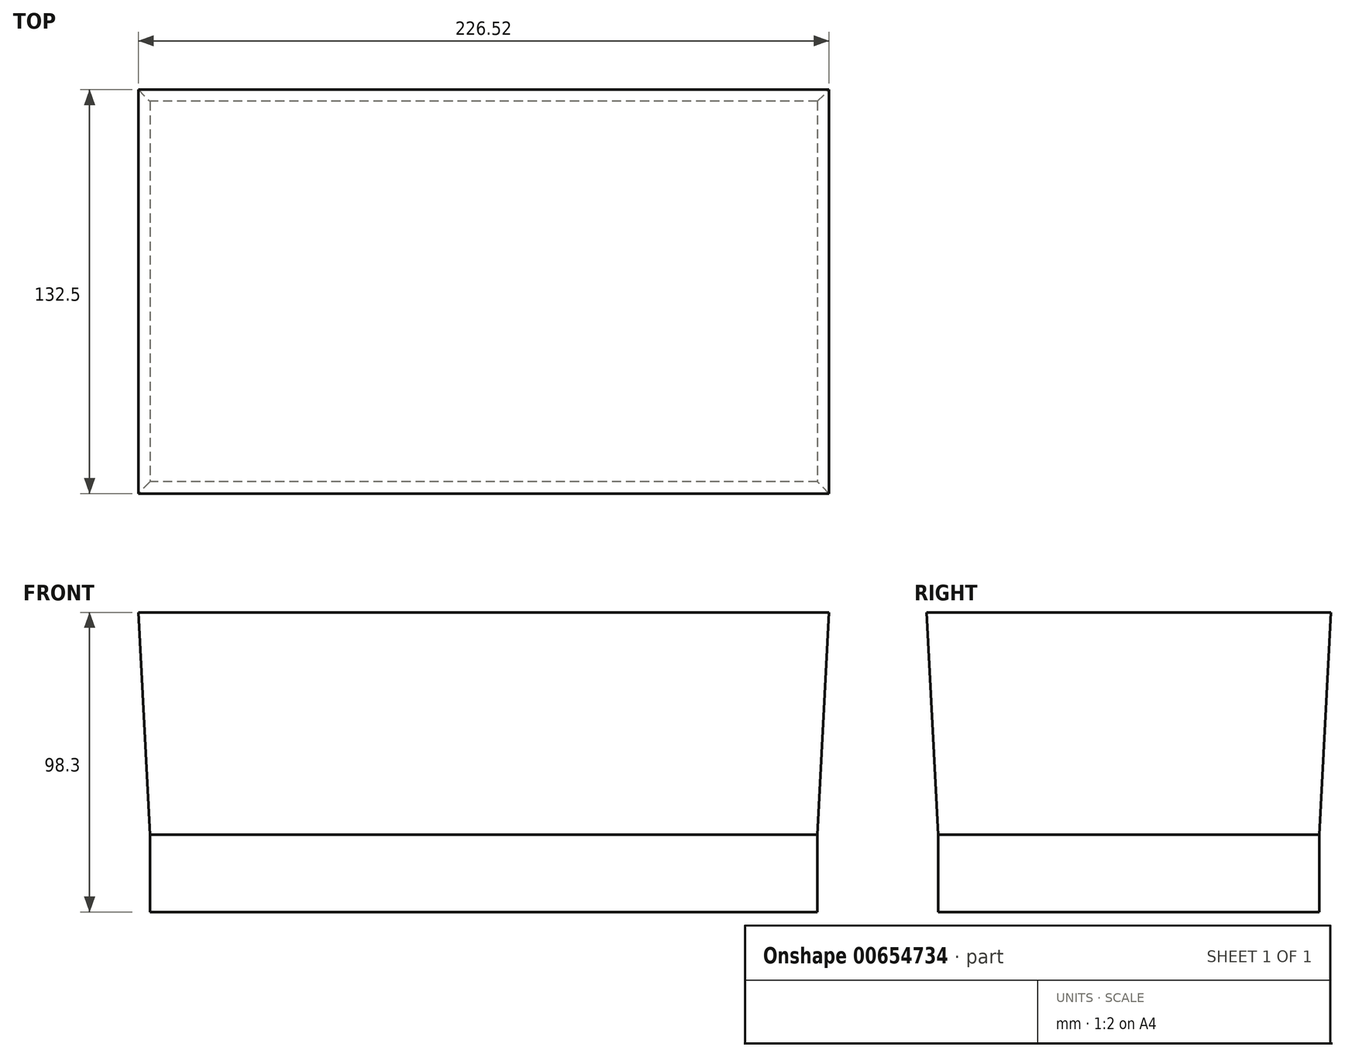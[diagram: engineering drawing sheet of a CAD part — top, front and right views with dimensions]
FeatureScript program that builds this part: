
annotation { "Feature Type Name" : "Feature", "Feature Type Description" : "" }
export const myFeature = defineFeature(function(context is Context, id is Id, definition is map)
    precondition{}
    {
        {
            var Q0;
            Q0=qCreatedBy(makeId("Top.planeOp"),FACE);
            var sketch = newSketch(context, id + "F0", { "sketchPlane" : qUnion([Q0])});
            skLineSegment(sketch, "E0.bottom", {"start": v(109.44, 62.43) * mm, "end": v(-109.44, 62.43) * mm});
            skLineSegment(sketch, "E0.top", {"start": v(109.44, -62.43) * mm, "end": v(-109.44, -62.43) * mm});
            skLineSegment(sketch, "E0.left", {"start": v(109.44, 62.43) * mm, "end": v(109.44, -62.43) * mm});
            skLineSegment(sketch, "E0.right", {"start": v(-109.44, 62.43) * mm, "end": v(-109.44, -62.43) * mm});
            skPoint(sketch, "E0.middle", {"position": v(0, 0) * mm});
            skSolve(sketch);
        }
        {
            var Q0;
            Q0 = qSketchRegion(id + "F0", true);
            extrude(context, id + "F1", {"entities" : qUnion([Q0]), "depth" : 72.9 * mm, "offsetDistance" : 25.4 * mm, "hasDraft" : true, "draftAngle" : 3 * degree, "hasSecondDirection" : true, "secondDirectionOppositeDirection" : true, "secondDirectionDepth" : 25.4 * mm});
        }
    });
